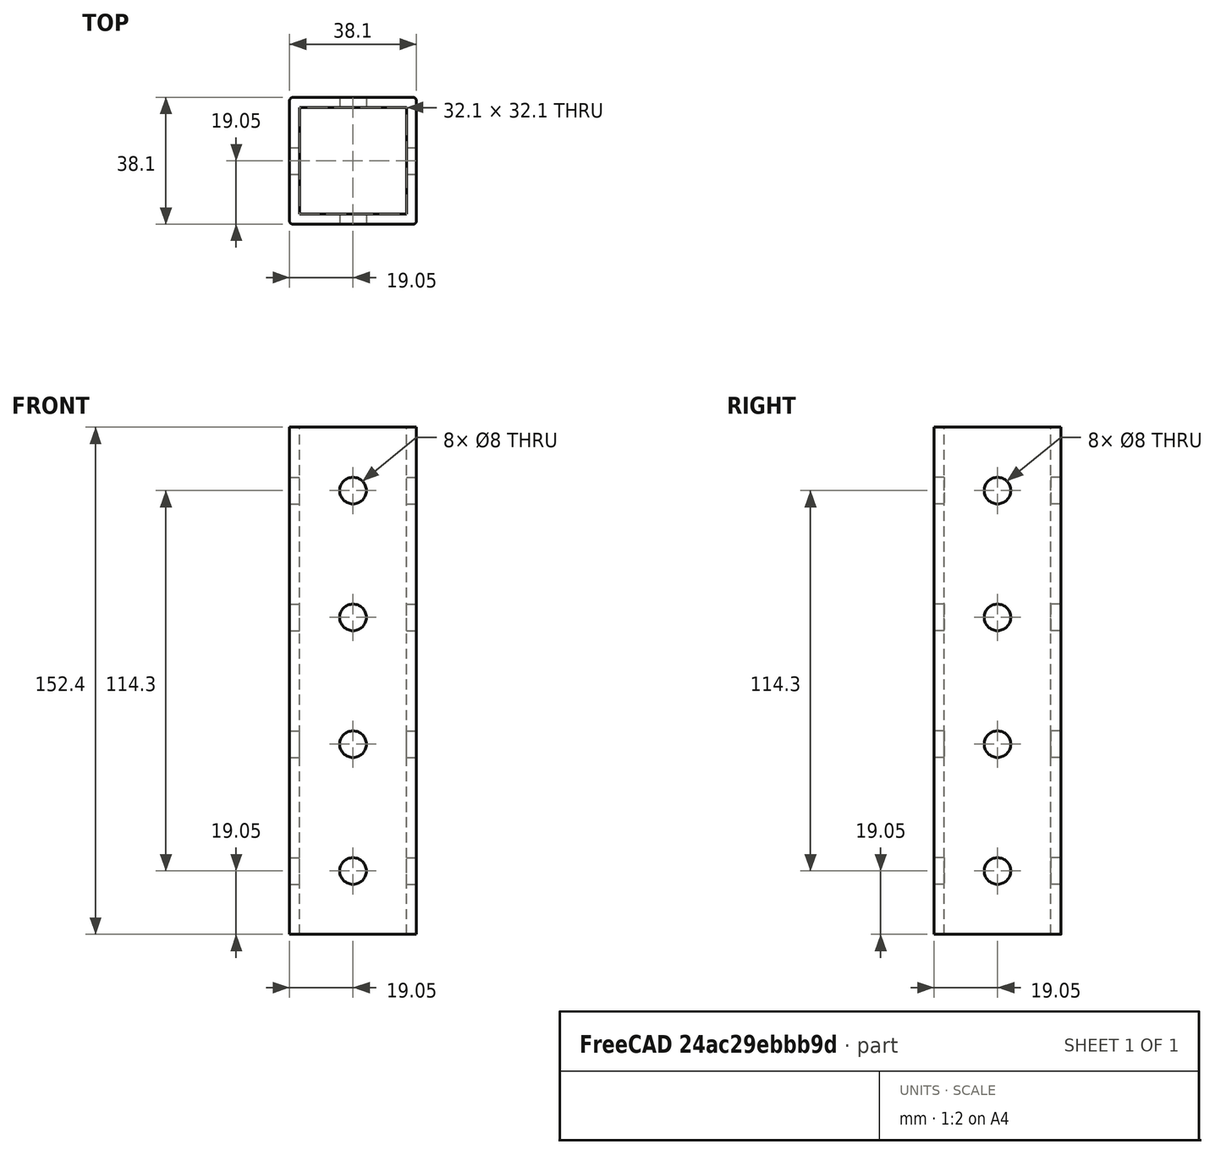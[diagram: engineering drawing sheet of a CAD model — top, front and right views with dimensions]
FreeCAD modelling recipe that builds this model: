
FCSTD DOCUMENT  (FreeCAD 0.15R4671 (Git))
Label: 4x-fillet-hollow
License: All rights reserved
LicenseURL: http://en.wikipedia.org/wiki/All_rights_reserved
objects: Part::Cut×3, Part::Box×2, Part::Cylinder×2, Part::FeaturePython×2, PartDesign::Fillet×1
note: 10 computed .brp shape members not serialized (recipe doc carries the construction recipe); baked Part::Feature solids carry a one-line shape summary decoded from their .brp

FEATURE [Part::Box] Box  label="Beam"
  Height = 152.4
  Length = 38.1
  Width = 38.1
FEATURE [Part::Cylinder] Cylinder
  Angle = 360
  Height = 38.1
  Placement = pos=(0,19.05,19.05) rot=(0,1,0;1.5708rad)
  Radius = 4
FEATURE [Part::Cylinder] Cylinder001
  Angle = 360
  Height = 38.1
  Placement = pos=(19.05,38.1,19.05) rot=(1,0,0;1.5708rad)
  Radius = 4
FEATURE [Part::FeaturePython] Array  label="Holes1"  # Draft array (typed FeaturePython)
  Angle = 360
  ArrayType = 0
  Axis = (0,0,1)
  Base = -> Cylinder001
  Center = (0,0,0)
  Fuse = false
  IntervalAxis = (0,0,0)
  IntervalX = (1,0,0)
  IntervalY = (0,1,0)
  IntervalZ = (0,0,38.1)
  NumberPolar = 1
  NumberX = 1
  NumberY = 1
  NumberZ = 4
FEATURE [Part::FeaturePython] Array001  label="Holes2"  # Draft array (typed FeaturePython)
  Angle = 360
  ArrayType = 0
  Axis = (0,0,1)
  Base = -> Cylinder
  Center = (0,0,0)
  Fuse = false
  IntervalAxis = (0,0,0)
  IntervalX = (1,0,0)
  IntervalY = (0,1,0)
  IntervalZ = (0,0,38.1)
  NumberPolar = 1
  NumberX = 1
  NumberY = 1
  NumberZ = 4
FEATURE [Part::Box] Box001  label="Cutout"
  Height = 152.4
  Length = 32.1
  Placement = pos=(3,3,0) rot=(0,0,1;0rad)
  Width = 32.1
FEATURE [PartDesign::Fillet] Fillet
  Base = -> Box [Edge1,Edge5,Edge7,Edge3]
  Radius = 1
FEATURE [Part::Cut] Cut
  Base = -> Fillet
  Tool = -> Array
FEATURE [Part::Cut] Cut001
  Base = -> Cut
  Tool = -> Array001
FEATURE [Part::Cut] Cut002
  Base = -> Cut001
  Tool = -> Box001
